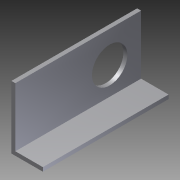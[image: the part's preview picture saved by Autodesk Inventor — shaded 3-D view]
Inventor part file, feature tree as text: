
AUTODESK INVENTOR PART (.ipt)
format: ipt  version: 2012 (Build 160160000, 160)  size: 88,064 bytes
history: native  units: in
note: dims shown in document units (in); Inventor stores cm internally (conversion verified against a paired STEP export)
features: extrude x2, sketch x2
ambient origin geometry x8: Origin, YZ Plane, XZ Plane, XY Plane, X Axis, Y Axis, Z Axis, Center Point
bodies: Solid1 (feature_tree)
feature tree (4):
  extrude  "Extrusion1"  Depth=1.0in
  extrude  "Extrusion2"  Depth=0.125in
  sketch  "Sketch1"  dims[d0=2.0in d1=1.0in]
  sketch  "Sketch2"  dims[d2=0.125in d3=0.125in d4=4.0in d5=0.0in d6=1.125in d7=1.0in d8=1.0in d9=4.0in d10=0.0in]
